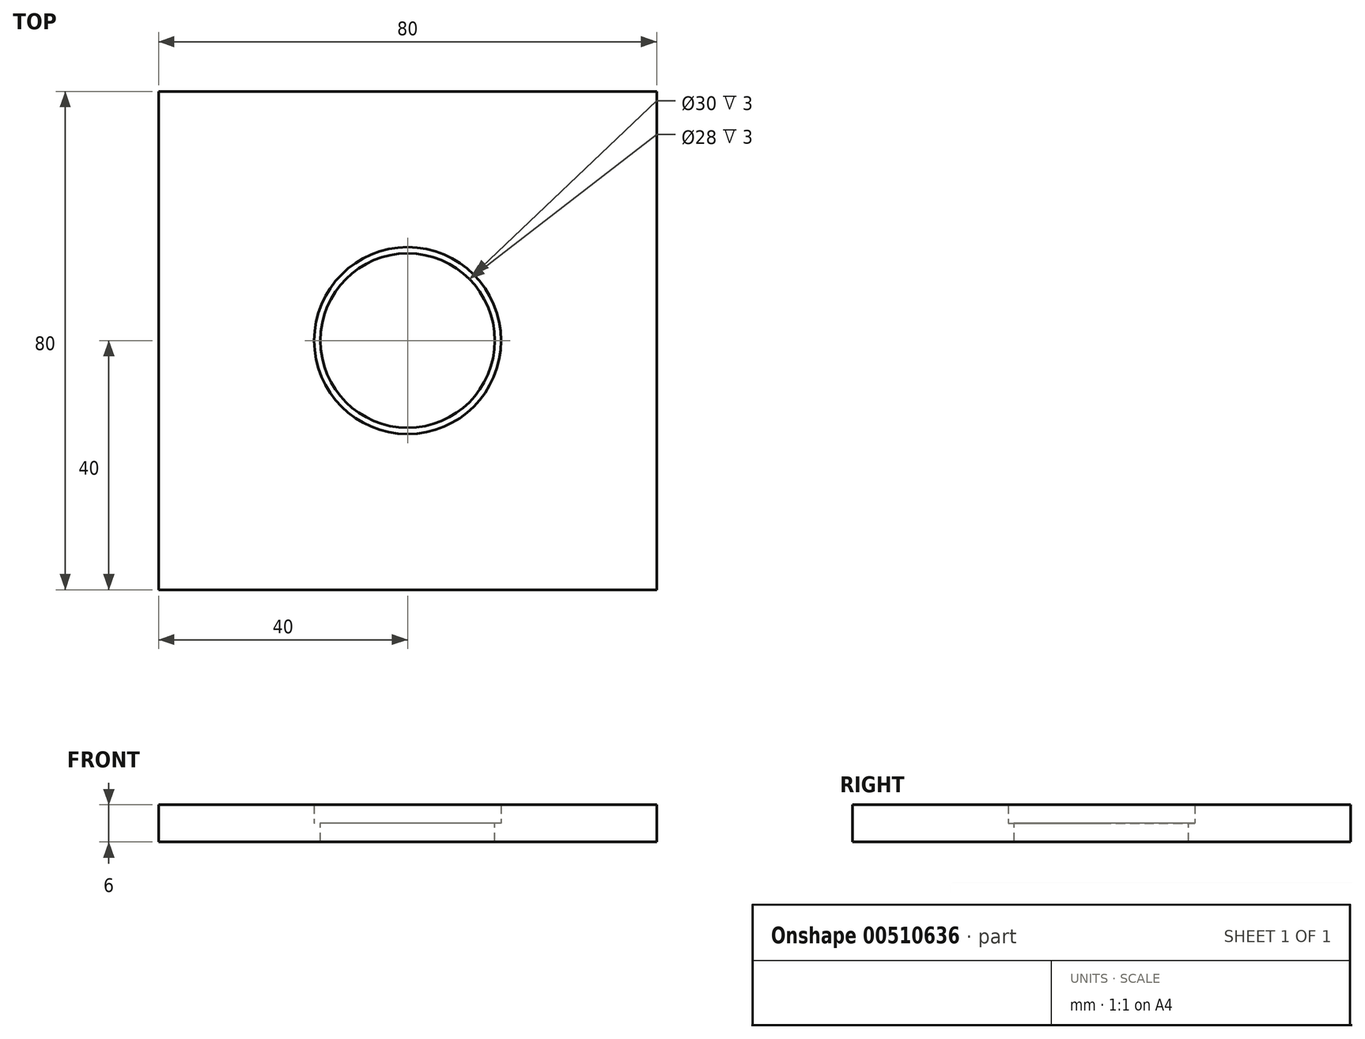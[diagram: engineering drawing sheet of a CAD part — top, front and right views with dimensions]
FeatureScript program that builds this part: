
annotation { "Feature Type Name" : "Feature", "Feature Type Description" : "" }
export const myFeature = defineFeature(function(context is Context, id is Id, definition is map)
    precondition{}
    {
        {
            var Q0;
            Q0=qCreatedBy(makeId("Top.planeOp"),FACE);
            var sketch = newSketch(context, id + "F0", { "sketchPlane" : qUnion([Q0])});
            skLineSegment(sketch, "E0.bottom", {"start": v(-40, 40) * mm, "end": v(40, 40) * mm});
            skLineSegment(sketch, "E0.top", {"start": v(-40, -40) * mm, "end": v(40, -40) * mm});
            skLineSegment(sketch, "E0.left", {"start": v(-40, 40) * mm, "end": v(-40, -40) * mm});
            skLineSegment(sketch, "E0.right", {"start": v(40, 40) * mm, "end": v(40, -40) * mm});
            skPoint(sketch, "E0.middle", {"position": v(0, 0) * mm});
            skCircle(sketch, "E1", {"center": v(0, 0) * mm, "radius": 14 * mm});
            skCircle(sketch, "E2", {"center": v(0, 0) * mm, "radius": 15 * mm});
            skSolve(sketch);
        }
        {
            var Q0;
            Q0 = qSketchRegion(id + "F0", true);
            extrude(context, id + "F1", {"entities" : qUnion([Q0]), "depth" : 3 * mm});
        }
        {
            var Q0;
            Q0 = qSketchRegion(id + "F0", true);
            var Q1;
            Q1=makeQuery(id+"F1.opExtrude","CAP_FACE",FACE,{"disambiguationData":[OSD([sQuery(id+"F0.wireOp",EDGE,"E0.bottom"),sQuery(id+"F0.wireOp",EDGE,"E0.top"),sQuery(id+"F0.wireOp",EDGE,"E0.left"),sQuery(id+"F0.wireOp",EDGE,"E0.right"),sQuery(id+"F0.wireOp",EDGE,"E1")])],"isStart":false});
            var Q2;
            Q2=makeQuery(id+"F0.imprint","IMPRINT",FACE,{"disambiguationData":[TD([[makeQuery(id+"F0.imprint","IMPRINT",EDGE,{"derivedFrom":sQuery(id+"F0.wireOp",EDGE,"E1")}),-1.0]])]});
            extrude(context, id + "F2", {"entities" : qUnion([Q0, Q1, Q2]), "operationType" : NewBodyOperationType.ADD, "oppositeDirection" : true, "depth" : 3 * mm});
        }
    });
